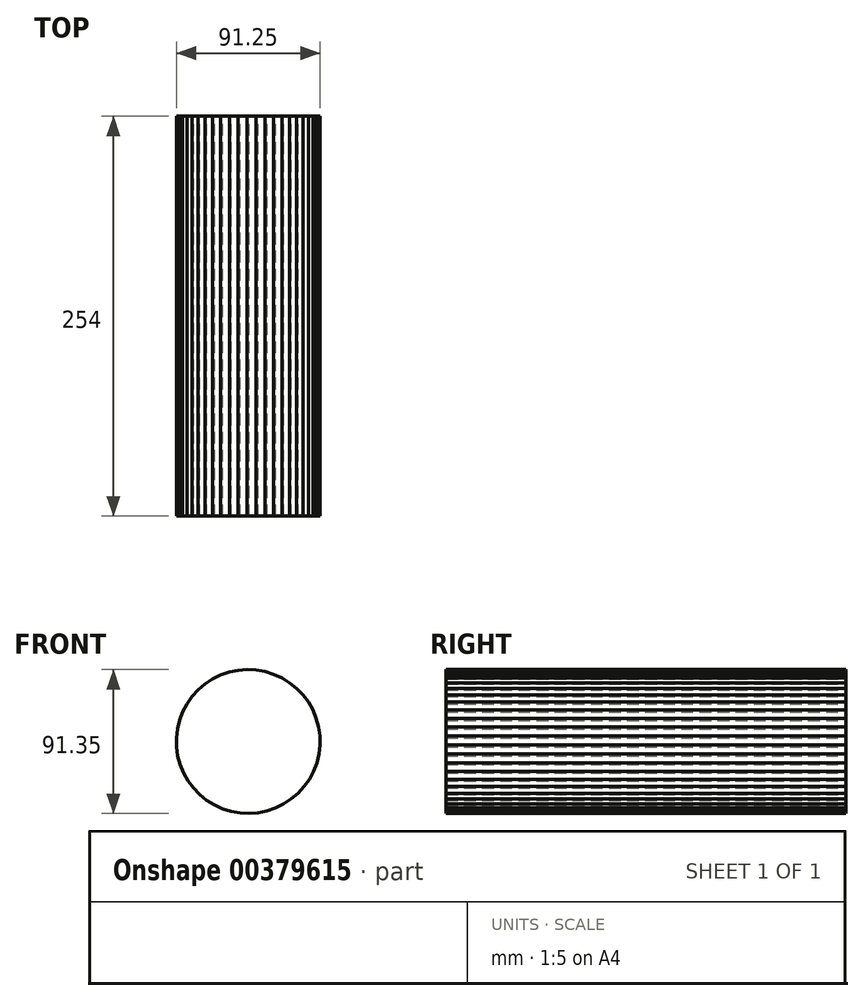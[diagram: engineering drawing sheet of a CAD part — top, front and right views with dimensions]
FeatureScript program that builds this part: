
annotation { "Feature Type Name" : "Feature", "Feature Type Description" : "" }
export const myFeature = defineFeature(function(context is Context, id is Id, definition is map)
    precondition{}
    {
        {
            var Q0;
            Q0=qCreatedBy(makeId("Front.planeOp"),FACE);
            var sketch = newSketch(context, id + "F0", { "sketchPlane" : qUnion([Q0])});
            skCircle(sketch, "E0", {"center": v(-11.57, 48.73) * mm, "radius": 12.91 * mm});
            skCircle(sketch, "E1.cCircle", {"center": v(-114.14, 37.35) * mm, "radius": 20.5 * mm, "construction": true});
            skLineSegment(sketch, "E1.0", {"start": v(-93.92, 33.67) * mm, "end": v(-94.54, 31.17) * mm});
            skLineSegment(sketch, "E1.1", {"start": v(-94.54, 31.17) * mm, "end": v(-95.47, 28.76) * mm});
            skLineSegment(sketch, "E1.2", {"start": v(-95.47, 28.76) * mm, "end": v(-96.7, 26.49) * mm});
            skLineSegment(sketch, "E1.3", {"start": v(-96.7, 26.49) * mm, "end": v(-98.2, 24.39) * mm});
            skLineSegment(sketch, "E1.4", {"start": v(-98.2, 24.39) * mm, "end": v(-99.94, 22.5) * mm});
            skLineSegment(sketch, "E1.5", {"start": v(-99.94, 22.5) * mm, "end": v(-101.92, 20.83) * mm});
            skLineSegment(sketch, "E1.6", {"start": v(-101.92, 20.83) * mm, "end": v(-104.08, 19.43) * mm});
            skLineSegment(sketch, "E1.7", {"start": v(-104.08, 19.43) * mm, "end": v(-106.4, 18.3) * mm});
            skLineSegment(sketch, "E1.8", {"start": v(-106.4, 18.3) * mm, "end": v(-108.86, 17.5) * mm});
            skLineSegment(sketch, "E1.9", {"start": v(-108.86, 17.5) * mm, "end": v(-111.39, 16.99) * mm});
            skLineSegment(sketch, "E1.10", {"start": v(-111.39, 16.99) * mm, "end": v(-113.96, 16.8) * mm});
            skLineSegment(sketch, "E1.11", {"start": v(-113.96, 16.8) * mm, "end": v(-116.54, 16.94) * mm});
            skLineSegment(sketch, "E1.12", {"start": v(-116.54, 16.94) * mm, "end": v(-119.08, 17.4) * mm});
            skLineSegment(sketch, "E1.13", {"start": v(-119.08, 17.4) * mm, "end": v(-121.54, 18.18) * mm});
            skLineSegment(sketch, "E1.14", {"start": v(-121.54, 18.18) * mm, "end": v(-123.88, 19.26) * mm});
            skLineSegment(sketch, "E1.15", {"start": v(-123.88, 19.26) * mm, "end": v(-126.07, 20.62) * mm});
            skLineSegment(sketch, "E1.16", {"start": v(-126.07, 20.62) * mm, "end": v(-128.08, 22.25) * mm});
            skLineSegment(sketch, "E1.17", {"start": v(-128.08, 22.25) * mm, "end": v(-129.86, 24.12) * mm});
            skLineSegment(sketch, "E1.18", {"start": v(-129.86, 24.12) * mm, "end": v(-131.4, 26.2) * mm});
            skLineSegment(sketch, "E1.19", {"start": v(-131.4, 26.2) * mm, "end": v(-132.66, 28.44) * mm});
            skLineSegment(sketch, "E1.20", {"start": v(-132.66, 28.44) * mm, "end": v(-133.63, 30.83) * mm});
            skLineSegment(sketch, "E1.21", {"start": v(-133.63, 30.83) * mm, "end": v(-134.29, 33.33) * mm});
            skLineSegment(sketch, "E1.22", {"start": v(-134.29, 33.33) * mm, "end": v(-134.63, 35.88) * mm});
            skLineSegment(sketch, "E1.23", {"start": v(-134.63, 35.88) * mm, "end": v(-134.66, 38.46) * mm});
            skLineSegment(sketch, "E1.24", {"start": v(-134.66, 38.46) * mm, "end": v(-134.36, 41.03) * mm});
            skLineSegment(sketch, "E1.25", {"start": v(-134.36, 41.03) * mm, "end": v(-133.74, 43.53) * mm});
            skLineSegment(sketch, "E1.26", {"start": v(-133.74, 43.53) * mm, "end": v(-132.8, 45.94) * mm});
            skLineSegment(sketch, "E1.27", {"start": v(-132.8, 45.94) * mm, "end": v(-131.58, 48.21) * mm});
            skLineSegment(sketch, "E1.28", {"start": v(-131.58, 48.21) * mm, "end": v(-130.08, 50.31) * mm});
            skLineSegment(sketch, "E1.29", {"start": v(-130.08, 50.31) * mm, "end": v(-128.33, 52.2) * mm});
            skLineSegment(sketch, "E1.30", {"start": v(-128.33, 52.2) * mm, "end": v(-126.36, 53.87) * mm});
            skLineSegment(sketch, "E1.31", {"start": v(-126.36, 53.87) * mm, "end": v(-124.2, 55.27) * mm});
            skLineSegment(sketch, "E1.32", {"start": v(-124.2, 55.27) * mm, "end": v(-121.87, 56.4) * mm});
            skLineSegment(sketch, "E1.33", {"start": v(-121.87, 56.4) * mm, "end": v(-119.42, 57.2) * mm});
            skLineSegment(sketch, "E1.34", {"start": v(-119.42, 57.2) * mm, "end": v(-116.89, 57.72) * mm});
            skLineSegment(sketch, "E1.35", {"start": v(-116.89, 57.72) * mm, "end": v(-114.31, 57.9) * mm});
            skLineSegment(sketch, "E1.36", {"start": v(-114.31, 57.9) * mm, "end": v(-111.74, 57.76) * mm});
            skLineSegment(sketch, "E1.37", {"start": v(-111.74, 57.76) * mm, "end": v(-109.2, 57.3) * mm});
            skLineSegment(sketch, "E1.38", {"start": v(-109.2, 57.3) * mm, "end": v(-106.74, 56.52) * mm});
            skLineSegment(sketch, "E1.39", {"start": v(-106.74, 56.52) * mm, "end": v(-104.4, 55.44) * mm});
            skLineSegment(sketch, "E1.40", {"start": v(-104.4, 55.44) * mm, "end": v(-102.2, 54.08) * mm});
            skLineSegment(sketch, "E1.41", {"start": v(-102.2, 54.08) * mm, "end": v(-100.2, 52.45) * mm});
            skLineSegment(sketch, "E1.42", {"start": v(-100.2, 52.45) * mm, "end": v(-98.42, 50.58) * mm});
            skLineSegment(sketch, "E1.43", {"start": v(-98.42, 50.58) * mm, "end": v(-96.88, 48.51) * mm});
            skLineSegment(sketch, "E1.44", {"start": v(-96.88, 48.51) * mm, "end": v(-95.62, 46.26) * mm});
            skLineSegment(sketch, "E1.45", {"start": v(-95.62, 46.26) * mm, "end": v(-94.65, 43.87) * mm});
            skLineSegment(sketch, "E1.46", {"start": v(-94.65, 43.87) * mm, "end": v(-93.99, 41.37) * mm});
            skLineSegment(sketch, "E1.47", {"start": v(-93.99, 41.37) * mm, "end": v(-93.64, 38.82) * mm});
            skLineSegment(sketch, "E1.48", {"start": v(-93.64, 38.82) * mm, "end": v(-93.62, 36.24) * mm});
            skLineSegment(sketch, "E1.49", {"start": v(-93.62, 36.24) * mm, "end": v(-93.92, 33.67) * mm});
            skPoint(sketch, "E1.0.midPoint", {"position": v(-94.23, 32.42) * mm});
            skCircle(sketch, "E2.cCircle", {"center": v(-114.14, 37.35) * mm, "radius": 33 * mm, "construction": true});
            skLineSegment(sketch, "E2.0", {"start": v(-93.3, 63.03) * mm, "end": v(-90.24, 60.21) * mm});
            skLineSegment(sketch, "E2.1", {"start": v(-90.24, 60.21) * mm, "end": v(-87.56, 57.04) * mm});
            skLineSegment(sketch, "E2.2", {"start": v(-87.56, 57.04) * mm, "end": v(-85.3, 53.55) * mm});
            skLineSegment(sketch, "E2.3", {"start": v(-85.3, 53.55) * mm, "end": v(-83.5, 49.8) * mm});
            skLineSegment(sketch, "E2.4", {"start": v(-83.5, 49.8) * mm, "end": v(-82.18, 45.87) * mm});
            skLineSegment(sketch, "E2.5", {"start": v(-82.18, 45.87) * mm, "end": v(-81.37, 41.8) * mm});
            skLineSegment(sketch, "E2.6", {"start": v(-81.37, 41.8) * mm, "end": v(-81.07, 37.66) * mm});
            skLineSegment(sketch, "E2.7", {"start": v(-81.07, 37.66) * mm, "end": v(-81.29, 33.5) * mm});
            skLineSegment(sketch, "E2.8", {"start": v(-81.29, 33.5) * mm, "end": v(-82.03, 29.42) * mm});
            skLineSegment(sketch, "E2.9", {"start": v(-82.03, 29.42) * mm, "end": v(-83.28, 25.46) * mm});
            skLineSegment(sketch, "E2.10", {"start": v(-83.28, 25.46) * mm, "end": v(-85.01, 21.69) * mm});
            skLineSegment(sketch, "E2.11", {"start": v(-85.01, 21.69) * mm, "end": v(-87.2, 18.16) * mm});
            skLineSegment(sketch, "E2.12", {"start": v(-87.2, 18.16) * mm, "end": v(-89.82, 14.93) * mm});
            skLineSegment(sketch, "E2.13", {"start": v(-89.82, 14.93) * mm, "end": v(-92.82, 12.06) * mm});
            skLineSegment(sketch, "E2.14", {"start": v(-92.82, 12.06) * mm, "end": v(-96.16, 9.6) * mm});
            skLineSegment(sketch, "E2.15", {"start": v(-96.16, 9.6) * mm, "end": v(-99.78, 7.56) * mm});
            skLineSegment(sketch, "E2.16", {"start": v(-99.78, 7.56) * mm, "end": v(-103.63, 6) * mm});
            skLineSegment(sketch, "E2.17", {"start": v(-103.63, 6) * mm, "end": v(-107.64, 4.92) * mm});
            skLineSegment(sketch, "E2.18", {"start": v(-107.64, 4.92) * mm, "end": v(-111.76, 4.36) * mm});
            skLineSegment(sketch, "E2.19", {"start": v(-111.76, 4.36) * mm, "end": v(-115.9, 4.33) * mm});
            skLineSegment(sketch, "E2.20", {"start": v(-115.9, 4.33) * mm, "end": v(-120.04, 4.8) * mm});
            skLineSegment(sketch, "E2.21", {"start": v(-120.04, 4.8) * mm, "end": v(-124.07, 5.8) * mm});
            skLineSegment(sketch, "E2.22", {"start": v(-124.07, 5.8) * mm, "end": v(-127.94, 7.3) * mm});
            skLineSegment(sketch, "E2.23", {"start": v(-127.94, 7.3) * mm, "end": v(-131.6, 9.26) * mm});
            skLineSegment(sketch, "E2.24", {"start": v(-131.6, 9.26) * mm, "end": v(-134.98, 11.67) * mm});
            skLineSegment(sketch, "E2.25", {"start": v(-134.98, 11.67) * mm, "end": v(-138.04, 14.49) * mm});
            skLineSegment(sketch, "E2.26", {"start": v(-138.04, 14.49) * mm, "end": v(-140.71, 17.67) * mm});
            skLineSegment(sketch, "E2.27", {"start": v(-140.71, 17.67) * mm, "end": v(-142.97, 21.15) * mm});
            skLineSegment(sketch, "E2.28", {"start": v(-142.97, 21.15) * mm, "end": v(-144.77, 24.9) * mm});
            skLineSegment(sketch, "E2.29", {"start": v(-144.77, 24.9) * mm, "end": v(-146.1, 28.83) * mm});
            skLineSegment(sketch, "E2.30", {"start": v(-146.1, 28.83) * mm, "end": v(-146.9, 32.9) * mm});
            skLineSegment(sketch, "E2.31", {"start": v(-146.9, 32.9) * mm, "end": v(-147.2, 37.05) * mm});
            skLineSegment(sketch, "E2.32", {"start": v(-147.2, 37.05) * mm, "end": v(-146.99, 41.2) * mm});
            skLineSegment(sketch, "E2.33", {"start": v(-146.99, 41.2) * mm, "end": v(-146.25, 45.28) * mm});
            skLineSegment(sketch, "E2.34", {"start": v(-146.25, 45.28) * mm, "end": v(-145, 49.24) * mm});
            skLineSegment(sketch, "E2.35", {"start": v(-145, 49.24) * mm, "end": v(-143.26, 53.02) * mm});
            skLineSegment(sketch, "E2.36", {"start": v(-143.26, 53.02) * mm, "end": v(-141.07, 56.54) * mm});
            skLineSegment(sketch, "E2.37", {"start": v(-141.07, 56.54) * mm, "end": v(-138.45, 59.77) * mm});
            skLineSegment(sketch, "E2.38", {"start": v(-138.45, 59.77) * mm, "end": v(-135.45, 62.64) * mm});
            skLineSegment(sketch, "E2.39", {"start": v(-135.45, 62.64) * mm, "end": v(-132.12, 65.11) * mm});
            skLineSegment(sketch, "E2.40", {"start": v(-132.12, 65.11) * mm, "end": v(-128.5, 67.14) * mm});
            skLineSegment(sketch, "E2.41", {"start": v(-128.5, 67.14) * mm, "end": v(-124.65, 68.7) * mm});
            skLineSegment(sketch, "E2.42", {"start": v(-124.65, 68.7) * mm, "end": v(-120.63, 69.78) * mm});
            skLineSegment(sketch, "E2.43", {"start": v(-120.63, 69.78) * mm, "end": v(-116.52, 70.34) * mm});
            skLineSegment(sketch, "E2.44", {"start": v(-116.52, 70.34) * mm, "end": v(-112.36, 70.38) * mm});
            skLineSegment(sketch, "E2.45", {"start": v(-112.36, 70.38) * mm, "end": v(-108.24, 69.9) * mm});
            skLineSegment(sketch, "E2.46", {"start": v(-108.24, 69.9) * mm, "end": v(-104.2, 68.9) * mm});
            skLineSegment(sketch, "E2.47", {"start": v(-104.2, 68.9) * mm, "end": v(-100.33, 67.4) * mm});
            skLineSegment(sketch, "E2.48", {"start": v(-100.33, 67.4) * mm, "end": v(-96.67, 65.44) * mm});
            skLineSegment(sketch, "E2.49", {"start": v(-96.67, 65.44) * mm, "end": v(-93.3, 63.03) * mm});
            skPoint(sketch, "E2.0.midPoint", {"position": v(-91.77, 61.62) * mm});
            skCircle(sketch, "E3.cCircle", {"center": v(-114.14, 37.35) * mm, "radius": 45.59 * mm, "construction": true});
            skLineSegment(sketch, "E3.0", {"start": v(-83.33, 71.08) * mm, "end": v(-79.35, 66.95) * mm});
            skLineSegment(sketch, "E3.1", {"start": v(-79.35, 66.95) * mm, "end": v(-75.9, 62.36) * mm});
            skLineSegment(sketch, "E3.2", {"start": v(-75.9, 62.36) * mm, "end": v(-73.08, 57.37) * mm});
            skLineSegment(sketch, "E3.3", {"start": v(-73.08, 57.37) * mm, "end": v(-70.9, 52.06) * mm});
            skLineSegment(sketch, "E3.4", {"start": v(-70.9, 52.06) * mm, "end": v(-69.39, 46.53) * mm});
            skLineSegment(sketch, "E3.5", {"start": v(-69.39, 46.53) * mm, "end": v(-68.6, 40.85) * mm});
            skLineSegment(sketch, "E3.6", {"start": v(-68.6, 40.85) * mm, "end": v(-68.51, 35.11) * mm});
            skLineSegment(sketch, "E3.7", {"start": v(-68.51, 35.11) * mm, "end": v(-69.15, 29.4) * mm});
            skLineSegment(sketch, "E3.8", {"start": v(-69.15, 29.4) * mm, "end": v(-70.5, 23.83) * mm});
            skLineSegment(sketch, "E3.9", {"start": v(-70.5, 23.83) * mm, "end": v(-72.54, 18.47) * mm});
            skLineSegment(sketch, "E3.10", {"start": v(-72.54, 18.47) * mm, "end": v(-75.24, 13.4) * mm});
            skLineSegment(sketch, "E3.11", {"start": v(-75.24, 13.4) * mm, "end": v(-78.54, 8.72) * mm});
            skLineSegment(sketch, "E3.12", {"start": v(-78.54, 8.72) * mm, "end": v(-82.41, 4.49) * mm});
            skLineSegment(sketch, "E3.13", {"start": v(-82.41, 4.49) * mm, "end": v(-86.78, 0.77) * mm});
            skLineSegment(sketch, "E3.14", {"start": v(-86.78, 0.77) * mm, "end": v(-91.58, -2.37) * mm});
            skLineSegment(sketch, "E3.15", {"start": v(-91.58, -2.37) * mm, "end": v(-96.74, -4.89) * mm});
            skLineSegment(sketch, "E3.16", {"start": v(-96.74, -4.89) * mm, "end": v(-102.17, -6.73) * mm});
            skLineSegment(sketch, "E3.17", {"start": v(-102.17, -6.73) * mm, "end": v(-107.79, -7.89) * mm});
            skLineSegment(sketch, "E3.18", {"start": v(-107.79, -7.89) * mm, "end": v(-113.5, -8.32) * mm});
            skLineSegment(sketch, "E3.19", {"start": v(-113.5, -8.32) * mm, "end": v(-119.24, -8.04) * mm});
            skLineSegment(sketch, "E3.20", {"start": v(-119.24, -8.04) * mm, "end": v(-124.89, -7.05) * mm});
            skLineSegment(sketch, "E3.21", {"start": v(-124.89, -7.05) * mm, "end": v(-130.37, -5.35) * mm});
            skLineSegment(sketch, "E3.22", {"start": v(-130.37, -5.35) * mm, "end": v(-135.6, -2.98) * mm});
            skLineSegment(sketch, "E3.23", {"start": v(-135.6, -2.98) * mm, "end": v(-140.48, 0.03) * mm});
            skLineSegment(sketch, "E3.24", {"start": v(-140.48, 0.03) * mm, "end": v(-144.95, 3.62) * mm});
            skLineSegment(sketch, "E3.25", {"start": v(-144.95, 3.62) * mm, "end": v(-148.93, 7.75) * mm});
            skLineSegment(sketch, "E3.26", {"start": v(-148.93, 7.75) * mm, "end": v(-152.37, 12.35) * mm});
            skLineSegment(sketch, "E3.27", {"start": v(-152.37, 12.35) * mm, "end": v(-155.2, 17.33) * mm});
            skLineSegment(sketch, "E3.28", {"start": v(-155.2, 17.33) * mm, "end": v(-157.38, 22.64) * mm});
            skLineSegment(sketch, "E3.29", {"start": v(-157.38, 22.64) * mm, "end": v(-158.89, 28.17) * mm});
            skLineSegment(sketch, "E3.30", {"start": v(-158.89, 28.17) * mm, "end": v(-159.68, 33.85) * mm});
            skLineSegment(sketch, "E3.31", {"start": v(-159.68, 33.85) * mm, "end": v(-159.76, 39.6) * mm});
            skLineSegment(sketch, "E3.32", {"start": v(-159.76, 39.6) * mm, "end": v(-159.12, 45.3) * mm});
            skLineSegment(sketch, "E3.33", {"start": v(-159.12, 45.3) * mm, "end": v(-157.77, 50.87) * mm});
            skLineSegment(sketch, "E3.34", {"start": v(-157.77, 50.87) * mm, "end": v(-155.73, 56.23) * mm});
            skLineSegment(sketch, "E3.35", {"start": v(-155.73, 56.23) * mm, "end": v(-153.04, 61.3) * mm});
            skLineSegment(sketch, "E3.36", {"start": v(-153.04, 61.3) * mm, "end": v(-149.73, 65.98) * mm});
            skLineSegment(sketch, "E3.37", {"start": v(-149.73, 65.98) * mm, "end": v(-145.86, 70.22) * mm});
            skLineSegment(sketch, "E3.38", {"start": v(-145.86, 70.22) * mm, "end": v(-141.5, 73.93) * mm});
            skLineSegment(sketch, "E3.39", {"start": v(-141.5, 73.93) * mm, "end": v(-136.7, 77.07) * mm});
            skLineSegment(sketch, "E3.40", {"start": v(-136.7, 77.07) * mm, "end": v(-131.54, 79.59) * mm});
            skLineSegment(sketch, "E3.41", {"start": v(-131.54, 79.59) * mm, "end": v(-126.1, 81.43) * mm});
            skLineSegment(sketch, "E3.42", {"start": v(-126.1, 81.43) * mm, "end": v(-120.49, 82.59) * mm});
            skLineSegment(sketch, "E3.43", {"start": v(-120.49, 82.59) * mm, "end": v(-114.77, 83.03) * mm});
            skLineSegment(sketch, "E3.44", {"start": v(-114.77, 83.03) * mm, "end": v(-109.04, 82.74) * mm});
            skLineSegment(sketch, "E3.45", {"start": v(-109.04, 82.74) * mm, "end": v(-103.39, 81.75) * mm});
            skLineSegment(sketch, "E3.46", {"start": v(-103.39, 81.75) * mm, "end": v(-97.9, 80.05) * mm});
            skLineSegment(sketch, "E3.47", {"start": v(-97.9, 80.05) * mm, "end": v(-92.68, 77.68) * mm});
            skLineSegment(sketch, "E3.48", {"start": v(-92.68, 77.68) * mm, "end": v(-87.8, 74.67) * mm});
            skLineSegment(sketch, "E3.49", {"start": v(-87.8, 74.67) * mm, "end": v(-83.33, 71.08) * mm});
            skPoint(sketch, "E3.0.midPoint", {"position": v(-81.34, 69.01) * mm});
            skSolve(sketch);
        }
        {
            var Q0;
            Q0=makeQuery(id+"F0.imprint","IMPRINT",FACE,{"disambiguationData":[TD([[makeQuery(id+"F0.imprint","IMPRINT",EDGE,{"derivedFrom":sQuery(id+"F0.wireOp",EDGE,"E1.0")}),1.0]])]});
            var Q1;
            Q1=makeQuery(id+"F0.imprint","IMPRINT",FACE,{"disambiguationData":[TD([[makeQuery(id+"F0.imprint","IMPRINT",EDGE,{"derivedFrom":sQuery(id+"F0.wireOp",EDGE,"E2.0")}),1.0]])]});
            var Q2;
            Q2=makeQuery(id+"F0.imprint","IMPRINT",FACE,{"disambiguationData":[TD([[makeQuery(id+"F0.imprint","IMPRINT",EDGE,{"derivedFrom":sQuery(id+"F0.wireOp",EDGE,"E1.0")}),-1.0]])]});
            extrude(context, id + "F1", {"entities" : qUnion([Q0, Q1, Q2]), "depth" : 254 * mm});
        }
    });
